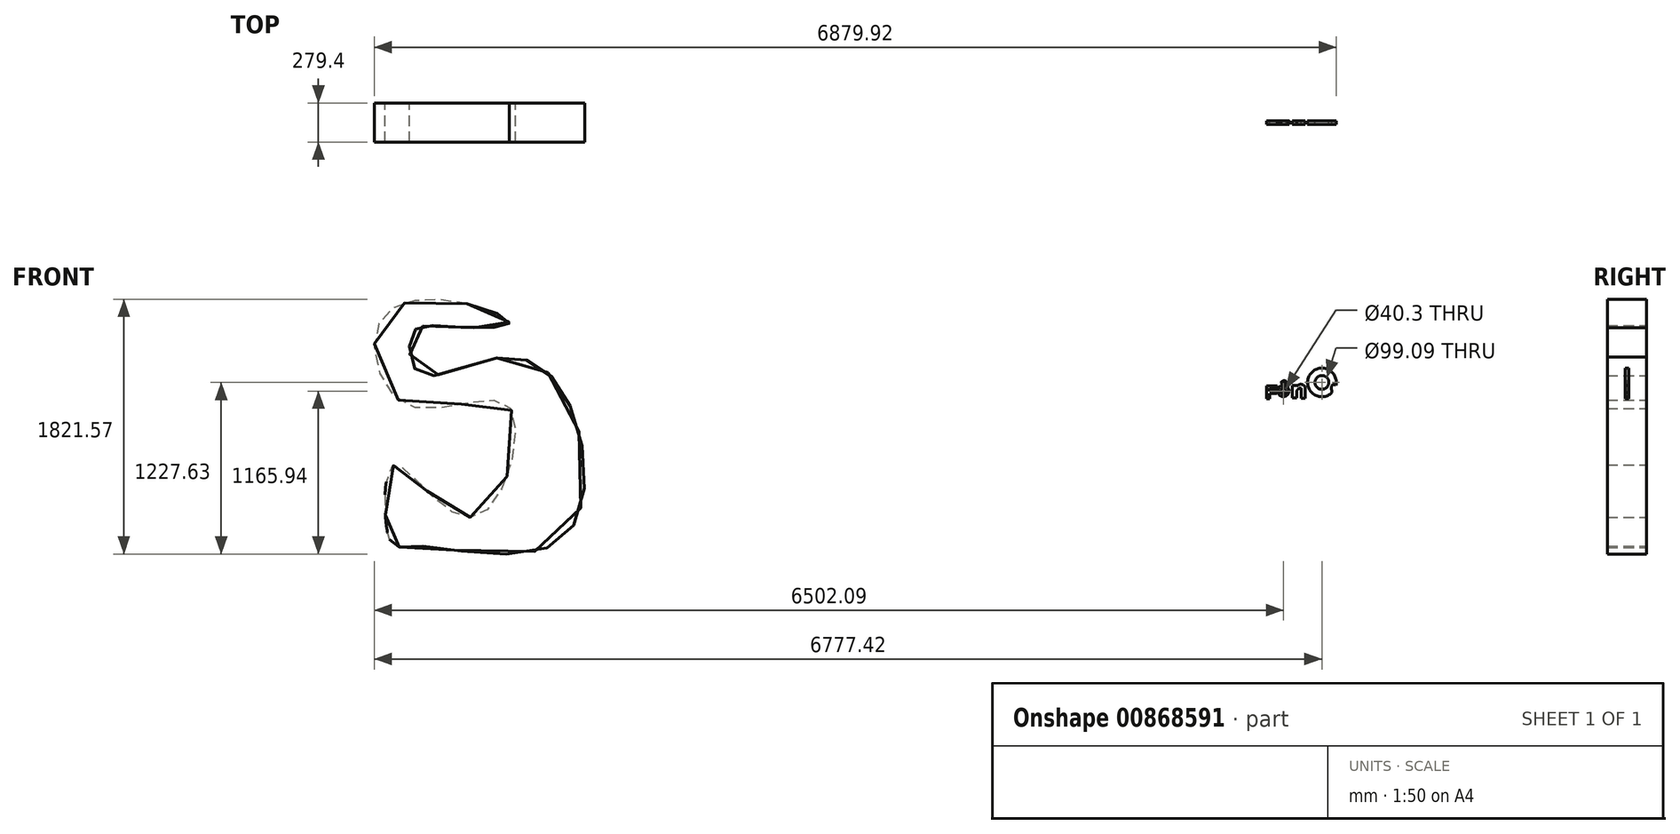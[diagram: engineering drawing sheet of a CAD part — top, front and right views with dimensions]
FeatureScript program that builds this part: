
annotation { "Feature Type Name" : "Feature", "Feature Type Description" : "" }
export const myFeature = defineFeature(function(context is Context, id is Id, definition is map)
    precondition{}
    {
        {
            var Q0;
            Q0=qCreatedBy(makeId("Front.planeOp"),FACE);
            var sketch = newSketch(context, id + "F0", { "sketchPlane" : qUnion([Q0])});
            skLineSegment(sketch, "E0.bottom", {"start": v(-50.8, 60.67) * mm, "end": v(4.9, 60.67) * mm});
            skLineSegment(sketch, "E0.top", {"start": v(-50.8, 44.4) * mm, "end": v(4.9, 44.4) * mm});
            skLineSegment(sketch, "E0.right", {"start": v(4.9, 60.67) * mm, "end": v(4.9, 44.4) * mm});
            skLineSegment(sketch, "E1.bottom", {"start": v(-50.8, 60.67) * mm, "end": v(-72.53, 60.67) * mm});
            skLineSegment(sketch, "E1.top", {"start": v(-50.8, -33.3) * mm, "end": v(-72.53, -33.3) * mm});
            skLineSegment(sketch, "E1.left", {"start": v(-50.8, 44.4) * mm, "end": v(-50.8, 22.81) * mm});
            skLineSegment(sketch, "E1.right", {"start": v(-72.53, 60.67) * mm, "end": v(-72.53, -33.3) * mm});
            skLineSegment(sketch, "E2.bottom", {"start": v(-50.8, 22.81) * mm, "end": v(0, 22.81) * mm});
            skLineSegment(sketch, "E2.top", {"start": v(-50.8, 6.25) * mm, "end": v(0, 6.25) * mm});
            skLineSegment(sketch, "E2.right", {"start": v(0, 22.81) * mm, "end": v(0, 6.25) * mm});
            skLineSegment(sketch, "E3.trimOffspring", {"start": v(-50.8, 6.25) * mm, "end": v(-50.8, -33.3) * mm});
            skSolve(sketch);
        }
        {
            var Q0;
            Q0=makeQuery(id+"F0.imprint","IMPRINT",FACE,{"disambiguationData":[TD([[makeQuery(id+"F0.imprint","IMPRINT",EDGE,{"derivedFrom":sQuery(id+"F0.wireOp",EDGE,"E0.bottom")}),-1.0]])]});
            extrude(context, id + "F1", {"entities" : qUnion([Q0]), "depth" : 25.4 * mm, "offsetDistance" : 25.4 * mm});
        }
        {
            var Q0;
            Q0=qCreatedBy(makeId("Front.planeOp"),FACE);
            var sketch = newSketch(context, id + "F2", { "sketchPlane" : qUnion([Q0])});
            skArc(sketch, "E4", {"start": v(69.2, 57.1) * mm, "mid": v(20.95, -7.07) * mm, "end": v(80.75, 46.5) * mm});
            skCircle(sketch, "E5", {"center": v(48.23, 22.64) * mm, "radius": 20.15 * mm});
            skArc(sketch, "E6", {"start": v(78.76, 79.15) * mm, "mid": v(54.45, 96.43) * mm, "end": v(28.9, 81.02) * mm});
            skArc(sketch, "E7", {"start": v(69.2, 71.88) * mm, "mid": v(55.51, 83.54) * mm, "end": v(39.92, 74.58) * mm});
            skLineSegment(sketch, "E8", {"start": v(69.2, 71.88) * mm, "end": v(69.2, 57.1) * mm});
            skLineSegment(sketch, "E9", {"start": v(80.75, 46.5) * mm, "end": v(78.76, 79.15) * mm});
            skLineSegment(sketch, "E10", {"start": v(39.92, 74.58) * mm, "end": v(28.9, 81.02) * mm});
            skSolve(sketch);
        }
        {
            var Q0;
            Q0=makeQuery(id+"F2.imprint","IMPRINT",FACE,{"disambiguationData":[TD([[makeQuery(id+"F2.imprint","IMPRINT",EDGE,{"derivedFrom":sQuery(id+"F2.wireOp",EDGE,"E4")}),1.0]])]});
            extrude(context, id + "F3", {"entities" : qUnion([Q0]), "depth" : 25.4 * mm, "offsetDistance" : 25.4 * mm});
        }
        {
            var Q0;
            Q0=qCreatedBy(makeId("Front.planeOp"),FACE);
            var sketch = newSketch(context, id + "F4", { "sketchPlane" : qUnion([Q0])});
            skLineSegment(sketch, "E11.bottom", {"start": v(111.56, 63.2) * mm, "end": v(143.56, 63.2) * mm});
            skLineSegment(sketch, "E11.top", {"start": v(111.56, -25.5) * mm, "end": v(143.56, -25.5) * mm});
            skLineSegment(sketch, "E11.left", {"start": v(111.56, 63.2) * mm, "end": v(111.56, -25.5) * mm});
            skLineSegment(sketch, "E11.right", {"start": v(143.56, 63.2) * mm, "end": v(143.56, 54.96) * mm});
            skArc(sketch, "E12", {"start": v(175.1, 42.83) * mm, "mid": v(154.4, 37.33) * mm, "end": v(143.56, 18.85) * mm});
            skPoint(sketch, "E12.startSnap0", {"position": v(143.56, 18.85) * mm});
            skArc(sketch, "E13", {"start": v(202.54, 53.6) * mm, "mid": v(173.44, 70.96) * mm, "end": v(143.56, 54.96) * mm});
            skLineSegment(sketch, "E14.top", {"start": v(202.54, -28.24) * mm, "end": v(175.1, -28.24) * mm});
            skLineSegment(sketch, "E14.left", {"start": v(202.54, 53.6) * mm, "end": v(202.54, -28.24) * mm});
            skLineSegment(sketch, "E14.right", {"start": v(175.1, 42.83) * mm, "end": v(175.1, -28.24) * mm});
            skPoint(sketch, "E15.orphan", {"position": v(199.34, 18.85) * mm});
            skLineSegment(sketch, "E16.trimOffspring", {"start": v(143.56, 18.85) * mm, "end": v(143.56, -25.5) * mm});
            skSolve(sketch);
        }
        {
            var Q0;
            Q0=makeQuery(id+"F4.imprint","IMPRINT",FACE,{"disambiguationData":[TD([[makeQuery(id+"F4.imprint","IMPRINT",EDGE,{"derivedFrom":sQuery(id+"F4.wireOp",EDGE,"E11.bottom")}),-1.0]])]});
            extrude(context, id + "F5", {"entities" : qUnion([Q0]), "depth" : 25.4 * mm, "offsetDistance" : 25.4 * mm});
        }
        {
            var Q0;
            Q0=qCreatedBy(makeId("Front.planeOp"),FACE);
            var sketch = newSketch(context, id + "F6", { "sketchPlane" : qUnion([Q0])});
            skArc(sketch, "E17", {"start": v(423.69, 62.4) * mm, "mid": v(233.81, 133.84) * mm, "end": v(395.52, 11.34) * mm});
            skCircle(sketch, "E18", {"center": v(323.56, 84.33) * mm, "radius": 49.55 * mm});
            skFitSpline(sketch, "E19", {"points": [v(395.52, 11.34) * mm, v(389.85, -115.47) * mm, v(295.16, -77.59) * mm, v(321.67, -49.18) * mm, v(253.5, -45.4) * mm, v(246.86, -122.1) * mm, v(425.83, -160.92) * mm, v(450.45, -111.68) * mm, v(423.69, 62.4) * mm, v(398.37, 66.34) * mm, v(395.52, 11.34) * mm]});
            skSolve(sketch);
        }
        {
            var Q0;
            Q0=makeQuery(id+"F6.imprint","IMPRINT",FACE,{"disambiguationData":[TD([[makeQuery(id+"F6.imprint","IMPRINT",EDGE,{"derivedFrom":sQuery(id+"F6.wireOp",EDGE,"E17")}),1.0]])]});
            extrude(context, id + "F7", {"entities" : qUnion([Q0]), "depth" : 25.4 * mm, "offsetDistance" : 25.4 * mm});
        }
        {
            var Q0;
            Q0=qCreatedBy(makeId("Front.planeOp"),FACE);
            var sketch = newSketch(context, id + "F8", { "sketchPlane" : qUnion([Q0])});
            skFitSpline(sketch, "E20", {"points": [v(-5789.87, 646.7) * mm, v(-6413.46, 521.99) * mm, v(-6212.53, -80.82) * mm, v(-5498.86, -80.82) * mm, v(-5658.23, -836.06) * mm, v(-6046.24, -725.2) * mm, v(-6330.32, -517.33) * mm, v(-6337.25, -1064.71) * mm, v(-6191.74, -1085.5) * mm, v(-5138.57, -1057.78) * mm, v(-5048.5, -94.68) * mm, v(-5533.5, 265.62) * mm, v(-6129.38, 147.83) * mm, v(-6184.81, 431.91) * mm, v(-5963.1, 487.34) * mm, v(-5491.93, 501.2) * mm, v(-5789.87, 646.7) * mm]});
            skSolve(sketch);
        }
        {
            var Q0;
            Q0=makeQuery(id+"F8.imprint","IMPRINT",FACE,{"disambiguationData":[TD([[makeQuery(id+"F8.imprint","IMPRINT",EDGE,{"derivedFrom":sQuery(id+"F8.wireOp",EDGE,"E20")}),1.0]])]});
            extrude(context, id + "F9", {"entities" : qUnion([Q0]), "depth" : 25.4 * mm, "offsetDistance" : 25.4 * mm});
        }
        {
            var Q0;
            Q0=makeQuery(id+"F9.opExtrude","CAP_FACE",FACE,{"disambiguationData":[OSD([sQuery(id+"F8.wireOp",EDGE,"E20")])],"isStart":false});
            extrude(context, id + "F10", {"entities" : qUnion([Q0]), "operationType" : NewBodyOperationType.ADD, "depth" : 127 * mm, "offsetDistance" : 25.4 * mm});
        }
        {
            var Q0;
            Q0=makeQuery(id+"F9.opExtrude","CAP_FACE",FACE,{"disambiguationData":[OSD([sQuery(id+"F8.wireOp",EDGE,"E20")])],"isStart":true});
            extrude(context, id + "F11", {"entities" : qUnion([Q0]), "operationType" : NewBodyOperationType.ADD, "depth" : 127 * mm, "offsetDistance" : 25.4 * mm});
        }
    });
